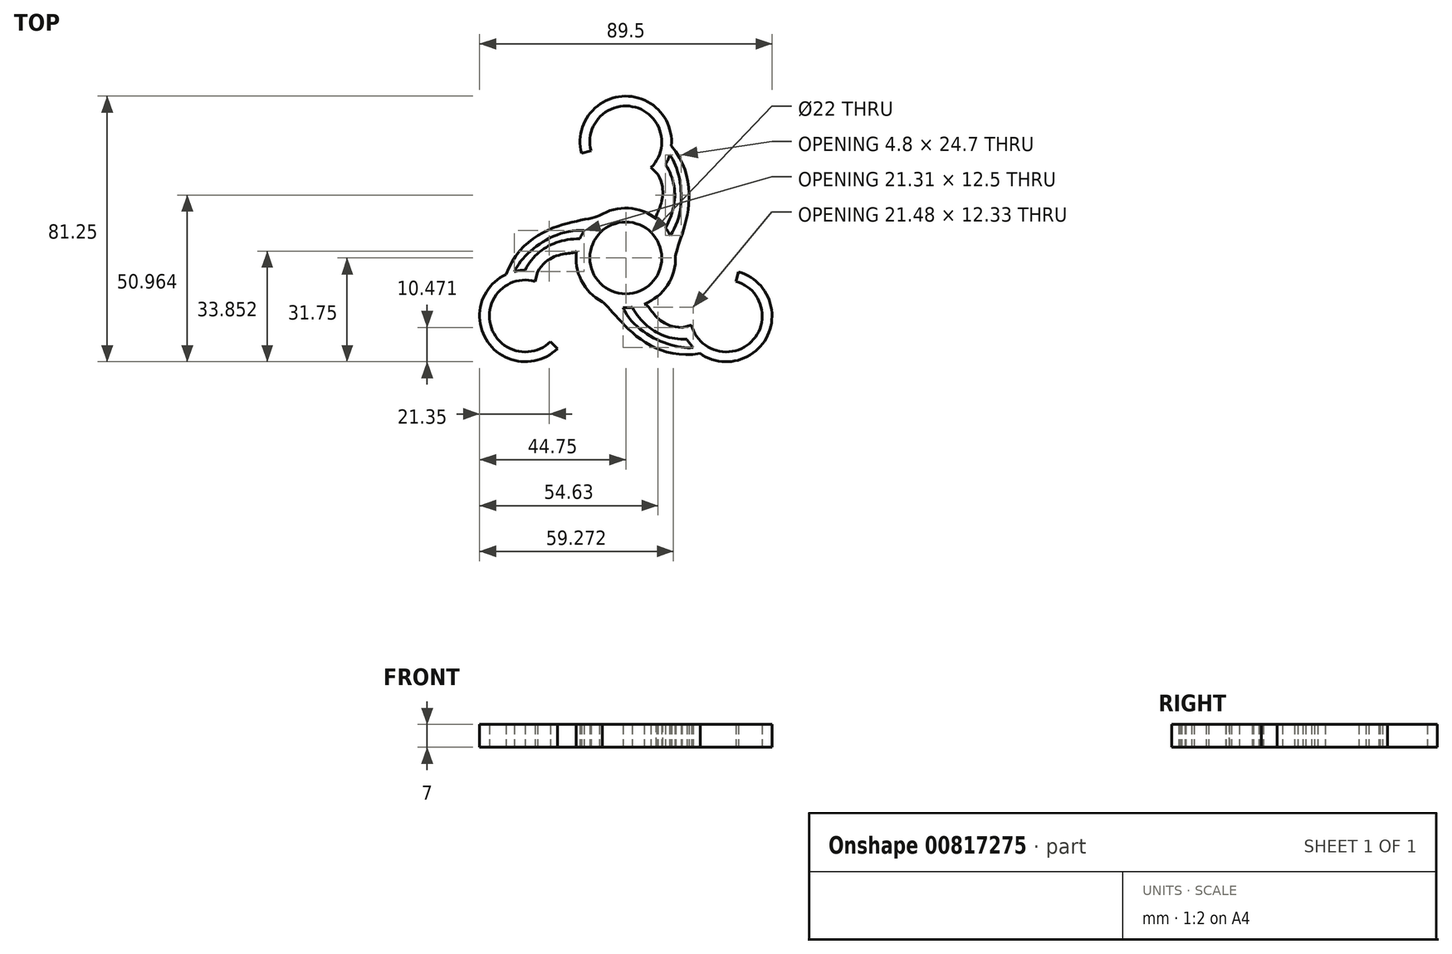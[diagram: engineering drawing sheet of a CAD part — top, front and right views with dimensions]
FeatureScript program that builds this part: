
annotation { "Feature Type Name" : "Feature", "Feature Type Description" : "" }
export const myFeature = defineFeature(function(context is Context, id is Id, definition is map)
    precondition{}
    {
        {
            var Q0;
            Q0=qCreatedBy(makeId("Top.planeOp"),FACE);
            var sketch = newSketch(context, id + "F0", { "sketchPlane" : qUnion([Q0])});
            skCircle(sketch, "E0", {"center": v(0, 0) * mm, "radius": 11 * mm});
            skPoint(sketch, "E1.endSnap0", {"position": v(0, 5.5) * mm});
            skLineSegment(sketch, "E2", {"start": v(0, 48.5) * mm, "end": v(0, 46.5) * mm});
            skLineSegment(sketch, "E3", {"start": v(0, 46.5) * mm, "end": v(0, 35.5) * mm});
            skArc(sketch, "E4", {"start": v(7.7, 27.66) * mm, "mid": v(2.94, 46.1) * mm, "end": v(-10.65, 32.75) * mm});
            skLineSegment(sketch, "E5", {"start": v(0, 35.5) * mm, "end": v(0, 39.5) * mm});
            skCircle(sketch, "E6", {"center": v(0, 35.5) * mm, "radius": 4 * mm});
            skCircle(sketch, "E7", {"center": v(0, 0) * mm, "radius": 15.24 * mm});
            skLineSegment(sketch, "E8", {"start": v(0, 48.5) * mm, "end": v(0, 49.5) * mm});
            skArc(sketch, "E9", {"start": v(9.81, 25.52) * mm, "mid": v(3.74, 49) * mm, "end": v(-13.55, 32) * mm});
            skArc(sketch, "E10.MirrorC", {"start": v(-23.04, -25.6) * mm, "mid": v(-41.4, -20.5) * mm, "end": v(-27.8, -7.15) * mm});
            skCircle(sketch, "E11.MirrorC", {"center": v(-30.75, -17.75) * mm, "radius": 4 * mm});
            skArc(sketch, "E12.MirrorC", {"start": v(-20.94, -27.74) * mm, "mid": v(-44.3, -21.26) * mm, "end": v(-27, -4.26) * mm});
            skCircle(sketch, "E13.MirrorC", {"center": v(30.75, -17.75) * mm, "radius": 4 * mm});
            skArc(sketch, "E14.MirrorC", {"start": v(33.69, -7.15) * mm, "mid": v(38.46, -25.6) * mm, "end": v(20.1, -20.5) * mm});
            skArc(sketch, "E15.MirrorC", {"start": v(34.5, -4.26) * mm, "mid": v(40.56, -27.74) * mm, "end": v(17.2, -21.26) * mm});
            skFitSpline(sketch, "E16", {"points": [v(15.24, 0) * mm, v(13.95, 34.3) * mm], "startDerivative": vector(-1.52, 11.68) * mm, "endDerivative": vector(-35.23, 42.9) * mm});
            skFitSpline(sketch, "E17", {"points": [v(9.5, 11.9) * mm, v(9.81, 25.52) * mm], "startDerivative": vector(-4.45, 3.14) * mm, "endDerivative": vector(-12.75, 22.22) * mm});
            skFitSpline(sketch, "E18", {"points": [v(12.12, 9.23) * mm, v(12.17, 28.59) * mm], "startDerivative": vector(11.06, 19.55) * mm, "endDerivative": vector(-11.71, 18.36) * mm});
            skFitSpline(sketch, "E19", {"points": [v(13.43, 31.57) * mm, v(13.6, 6.86) * mm], "startDerivative": vector(11.14, -15.04) * mm, "endDerivative": vector(-16.06, -22.56) * mm});
            skFitSpline(sketch, "E20.MirrorCS", {"points": [v(5.56, -14.19) * mm, v(17.2, -21.26) * mm], "startDerivative": vector(4.94, 2.29) * mm, "endDerivative": vector(25.62, -0.07) * mm});
            skFitSpline(sketch, "E21.MirrorCS", {"points": [v(20.62, -27.42) * mm, v(-0.86, -15.21) * mm], "startDerivative": vector(-18.6, -2.13) * mm, "endDerivative": vector(-11.5, 25.2) * mm});
            skFitSpline(sketch, "E22.MirrorCS", {"points": [v(-7.62, -13.2) * mm, v(22.73, -29.23) * mm], "startDerivative": vector(10.87, -4.52) * mm, "endDerivative": vector(54.76, 9.06) * mm});
            skFitSpline(sketch, "E23.MirrorCS", {"points": [v(1.93, -15.12) * mm, v(18.67, -24.84) * mm], "startDerivative": vector(11.4, -19.35) * mm, "endDerivative": vector(21.76, 0.97) * mm});
            skFitSpline(sketch, "E24.MirrorCS", {"points": [v(-15.07, 2.28) * mm, v(-27, -4.26) * mm], "startDerivative": vector(-0.5, -5.42) * mm, "endDerivative": vector(-12.87, -22.16) * mm});
            skFitSpline(sketch, "E25.MirrorCS", {"points": [v(-14.06, 5.88) * mm, v(-30.84, -3.75) * mm], "startDerivative": vector(-22.46, -0.2) * mm, "endDerivative": vector(-10.04, -19.32) * mm});
            skFitSpline(sketch, "E26.MirrorCS", {"points": [v(-34.05, -4.15) * mm, v(-12.75, 8.35) * mm], "startDerivative": vector(7.46, 17.17) * mm, "endDerivative": vector(27.57, -2.63) * mm});
            skFitSpline(sketch, "E27.MirrorCS", {"points": [v(-7.62, 13.2) * mm, v(-36.68, -5.07) * mm], "startDerivative": vector(-9.35, -7.15) * mm, "endDerivative": vector(-19.53, -51.96) * mm});
            skLineSegment(sketch, "E28", {"start": v(9.81, 25.52) * mm, "end": v(0, 35.5) * mm});
            skLineSegment(sketch, "E29", {"start": v(0, 35.5) * mm, "end": v(-13.55, 32) * mm});
            skLineSegment(sketch, "E30", {"start": v(-27, -4.26) * mm, "end": v(-30.75, -17.75) * mm});
            skLineSegment(sketch, "E31", {"start": v(17.2, -21.26) * mm, "end": v(30.75, -17.75) * mm});
            skLineSegment(sketch, "E32", {"start": v(30.75, -17.75) * mm, "end": v(34.5, -4.26) * mm});
            skLineSegment(sketch, "E33", {"start": v(-30.75, -17.75) * mm, "end": v(-20.94, -27.74) * mm});
            skSolve(sketch);
        }
        {
            var Q0;
            Q0=qSketchRegion(id+"F0",true);
            extrude(context, id + "F1", {"entities" : qUnion([Q0]), "depth" : 7 * mm, "offsetDistance" : 25 * mm});
        }
        {
            var Q0;
            Q0=sQuery(id+"F0.wireOp",VERTEX,"E3.end");
            var Q1;
            Q1=sQuery(id+"F0.wireOp",VERTEX,"E31.end");
            var Q2;
            Q2=sQuery(id+"F0.wireOp",VERTEX,"E30.end");
            var Q3;
            Q3=makeQuery(id+"F1.opExtrude","SWEPT_BODY",BODY,{"disambiguationData":[OSD([sQuery(id+"F0.wireOp",EDGE,"E0"),sQuery(id+"F0.wireOp",EDGE,"E6"),sQuery(id+"F0.wireOp",EDGE,"E7"),sQuery(id+"F0.wireOp",EDGE,"E9"),sQuery(id+"F0.wireOp",EDGE,"E11.MirrorC"),sQuery(id+"F0.wireOp",EDGE,"E12.MirrorC"),sQuery(id+"F0.wireOp",EDGE,"E13.MirrorC"),sQuery(id+"F0.wireOp",EDGE,"E15.MirrorC"),sQuery(id+"F0.wireOp",EDGE,"E16"),sQuery(id+"F0.wireOp",EDGE,"E17"),sQuery(id+"F0.wireOp",EDGE,"E18"),sQuery(id+"F0.wireOp",EDGE,"E19"),sQuery(id+"F0.wireOp",EDGE,"E20.MirrorCS"),sQuery(id+"F0.wireOp",EDGE,"E21.MirrorCS"),sQuery(id+"F0.wireOp",EDGE,"E22.MirrorCS"),sQuery(id+"F0.wireOp",EDGE,"E23.MirrorCS"),sQuery(id+"F0.wireOp",EDGE,"E24.MirrorCS"),sQuery(id+"F0.wireOp",EDGE,"E25.MirrorCS"),sQuery(id+"F0.wireOp",EDGE,"E26.MirrorCS"),sQuery(id+"F0.wireOp",EDGE,"E27.MirrorCS"),sQuery(id+"F0.wireOp",EDGE,"E28"),sQuery(id+"F0.wireOp",EDGE,"E29"),sQuery(id+"F0.wireOp",EDGE,"E30"),sQuery(id+"F0.wireOp",EDGE,"E31"),sQuery(id+"F0.wireOp",EDGE,"E32"),sQuery(id+"F0.wireOp",EDGE,"E33")])]});
            hole(context, id + "F2", {"style" : HoleStyle.SIMPLE, "endStyle" : HoleEndStyle.THROUGH, "oppositeDirection" : true, "holeDiameter" : 22 * mm, "majorDiameter" : 5 * mm, "isTappedThrough" : true, "tappedDepth" : 12 * mm, "tapClearance" : 3, "locations" : qUnion([Q0, Q1, Q2]), "scope" : qUnion([Q3])});
        }
    });
